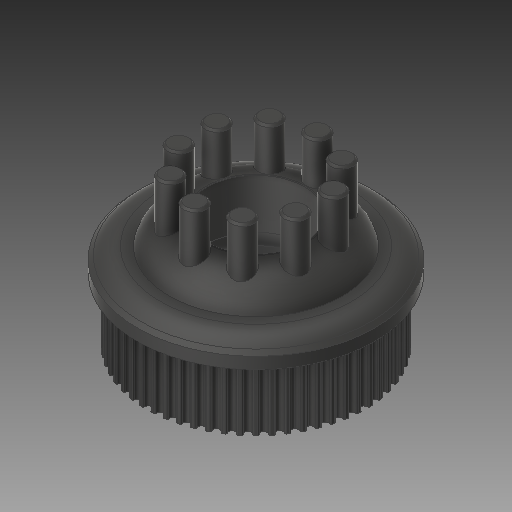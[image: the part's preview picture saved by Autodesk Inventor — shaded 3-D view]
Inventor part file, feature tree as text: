
AUTODESK INVENTOR PART (.ipt)
format: ipt  version: 2019.4 (Build 234330000, 330)  size: 971,776 bytes
history: native  units: mm
features: sketch x6, extrude x5, chamfer x4, fillet x3, other x1, pattern_circular x1, plane x1
ambient origin geometry x8: Origin, YZ Plane, XZ Plane, XY Plane, X Axis, Y Axis, Z Axis, Center Point
bodies: Solid1 (feature_tree)
feature tree (21):
  other  "gates_P60-3M-09AL.ipt"
  extrude  "Extrusion1"  Depth=7.0mm
  fillet  "Fillet1"  Radius=7.0mm
  extrude  "Extrusion2"  Depth=10.0mm
  chamfer  "Chamfer1"  Distance=18.0mm
  pattern_circular  "Circular Pattern1"  Count=10 Angle=360.0deg
  plane  "Work Plane1"
  sketch  "Sketch3"  dims[d9=0.5mm d10=2.0mm d11=45.0deg d12=100.0mm d13=360.0deg]
  extrude  "Extrusion3"  Depth=0.938mm
  chamfer  "Chamfer2"  Distance=2.4mm
  extrude  "Extrusion8"  Depth=7.0mm TaperAngle=0.0deg
  extrude  "Extrusion9"  Depth=7.0mm TaperAngle=45.0deg
  chamfer  "Chamfer5"  Distance=1.2mm
  fillet  "Fillet4"  Radius=10.0mm
  chamfer  "Chamfer6"  Distance=56.54mm
  fillet  "Fillet5"  Radius=11.0mm
  sketch  "Sketch1"  dims[d0=44.8mm d1=25.0mm d2=7.0mm d3=0.0mm]
  sketch  "Sketch2"  dims[d6=15.85mm d7=18.0mm d8=0.0mm]
  sketch  "Sketch4"  dims[d15=20.0mm d16=0.938mm]
  sketch  "Sketch2_1"  dims[d4=10.0mm d5=5.8mm]
  sketch  "Sketch11"  dims[d17=23.873241mm d18=2.4mm d19=7.0mm d20=0.0mm d24=2.4mm d25=1.0mm d26=45.0deg d50=1.2mm d52=10.0mm d53=56.54mm d54=11.0mm d55=0.0mm d56=10.0mm d57=0.0mm d60=3.0mm d61=2.0mm d62=45.0deg d63=7.0mm d71=9.5mm d72=14.65mm d73=45.0deg d74=7.0mm d75=5.0mm d76=0.0mm]
